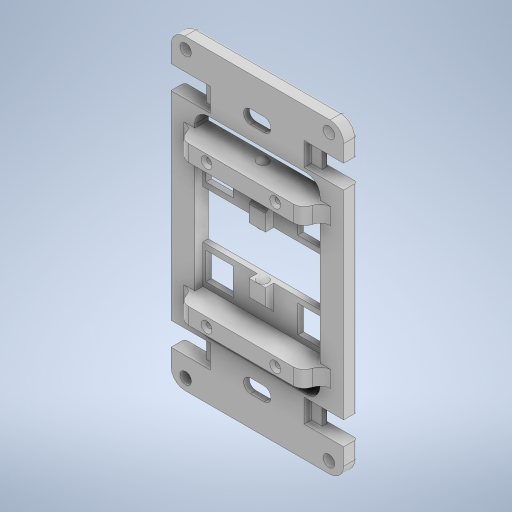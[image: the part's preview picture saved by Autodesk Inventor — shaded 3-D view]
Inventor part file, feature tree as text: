
AUTODESK INVENTOR PART (.ipt)
format: ipt  version: 2023 (Build 270158000, 158)  size: 619,008 bytes
history: native  units: mm
features: extrude x12, sketch x12, fillet x6, other x3, mirror x3, chamfer x2, revolve x1, projected_geometry x1
ambient origin geometry x8: Origin, YZ Plane, XZ Plane, XY Plane, X Axis, Y Axis, Z Axis, Center Point
bodies: Body1 (feature_tree)
feature tree (40):
  other  "솔리드1"
  extrude  "돌출1"  Depth=63.1mm
  extrude  "돌출2"  Depth=112.2mm
  extrude  "돌출3"  Depth=45.85mm
  fillet  "모깎기1"  Radius=70.23mm
  sketch  "스케치4"
  extrude  "돌출4"  Depth=5.0mm TaperAngle=0.0deg
  extrude  "돌출5"  Depth=5.0mm
  mirror  "미러1"
  mirror  "미러2"
  extrude  "돌출6"  Depth=5.0mm
  fillet  "모깎기2"  Radius=5.0mm
  mirror  "미러3"
  fillet  "모깎기3"  Radius=10.0mm
  other  "작업 평면1"
  sketch  "스케치9"
  extrude  "돌출8"  Depth=104.0mm
  extrude  "돌출9"  Depth=4.2mm
  fillet  "모깎기7"  Radius=52.4mm
  chamfer  "모따기1"  [1 undecoded]
  other  "작업 평면2"
  extrude  "돌출10"  Depth=5.0mm
  fillet  "모깎기9"  Radius=7.0mm
  fillet  "모깎기10"  Radius=8.5mm
  extrude  "돌출11"  Depth=3.4mm
  extrude  "돌출12"  Depth=11.2mm
  chamfer  "모따기2"  Distance=4.0mm
  revolve  "회전3"
  sketch  "스케치18"
  extrude  "돌출13"  TaperAngle=0.0deg  [1 undecoded]
  sketch  "스케치1"
  sketch  "스케치2"
  sketch  "스케치3"
  sketch  "스케치6"
  projected_geometry  "투영된 루프1"
  sketch  "스케치13"
  sketch  "스케치15"
  sketch  "스케치16"
  sketch  "스케치17"
  sketch  "스케치19"
note: 2 required parameter values undecoded (feature->parameter linkage not recoverable at this tier; creation-order binding heuristic only, values carry confidence <= 0.55)
